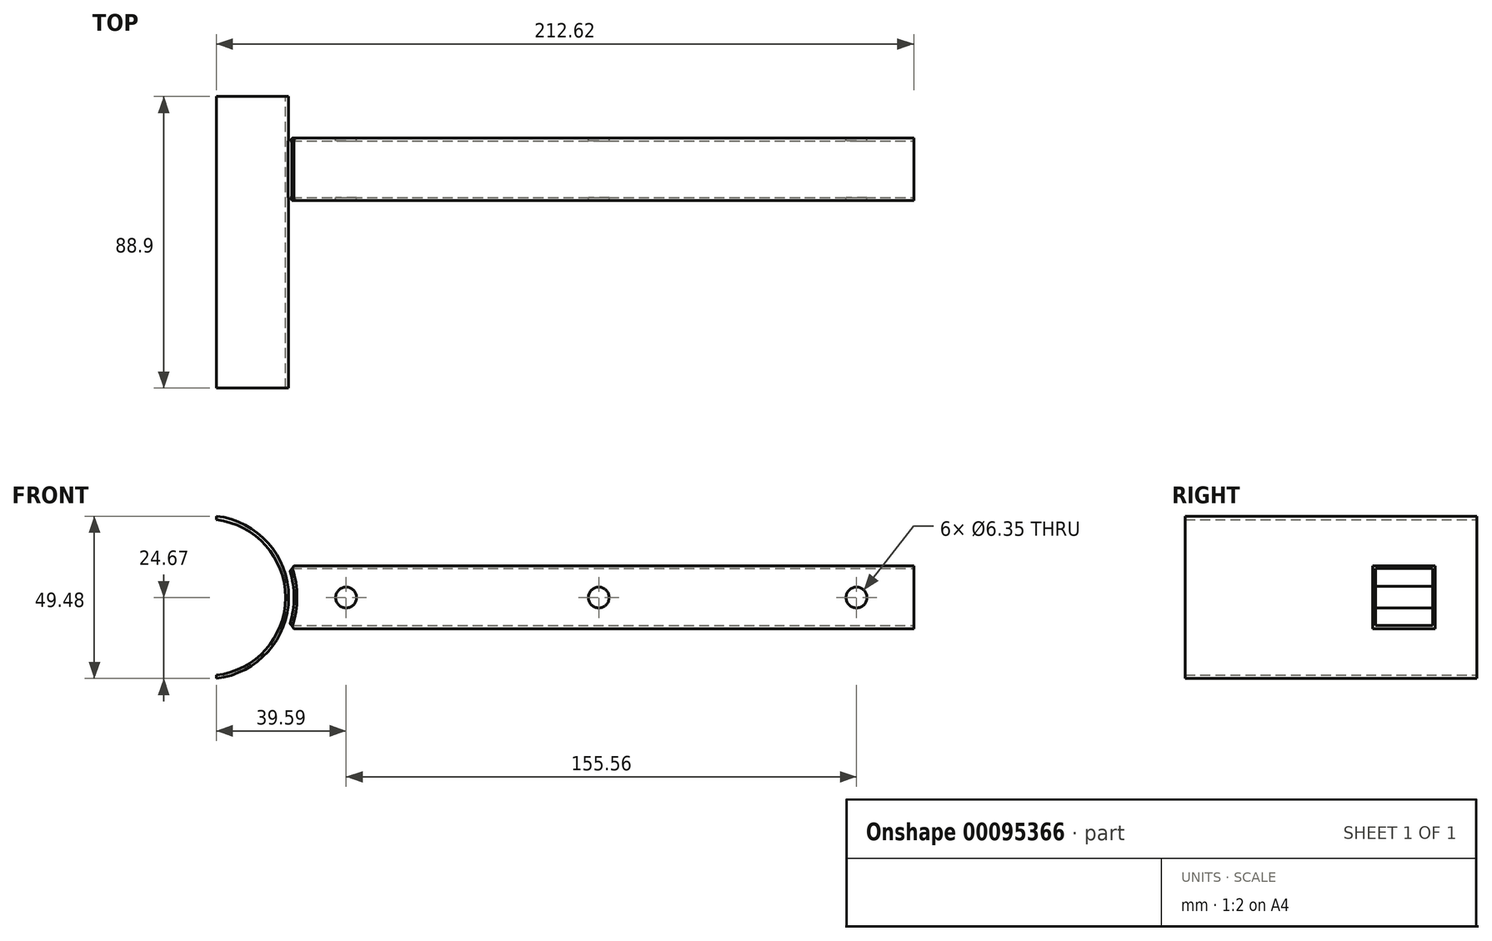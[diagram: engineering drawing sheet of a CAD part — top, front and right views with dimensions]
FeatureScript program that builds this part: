
annotation { "Feature Type Name" : "Feature", "Feature Type Description" : "" }
export const myFeature = defineFeature(function(context is Context, id is Id, definition is map)
    precondition{}
    {
        {
            var Q0;
            Q0=qCreatedBy(makeId("Front.planeOp"),FACE);
            cPlane(context, id + "F0", {"entities" : qUnion([Q0]), "cplaneType" : CPlaneType.OFFSET, "offset" : 12.7 * mm, "width" : 152.4 * mm, "height" : 152.4 * mm});
        }
        {
            var Q0;
            Q0=qCreatedBy(id+"F0.planeOp",FACE);
            var sketch = newSketch(context, id + "F1", { "sketchPlane" : qUnion([Q0])});
            skLineSegment(sketch, "E0.bottom", {"start": v(22.87, -9.48) * mm, "end": v(215.32, -9.48) * mm});
            skLineSegment(sketch, "E0.top", {"start": v(22.87, 9.62) * mm, "end": v(215.32, 9.62) * mm});
            skLineSegment(sketch, "E0.right", {"start": v(215.32, -9.48) * mm, "end": v(215.32, 9.62) * mm});
            skArc(sketch, "E1", {"start": v(22.87, -9.48) * mm, "mid": v(24.77, 0.07) * mm, "end": v(22.87, 9.62) * mm});
            skLineSegment(sketch, "E2", {"start": v(24.82, -9.48) * mm, "end": v(24.73, 9.62) * mm, "construction": true});
            skLineSegment(sketch, "E3", {"start": v(0, 0) * mm, "end": v(85.8, 0.07) * mm, "construction": true});
            skSolve(sketch);
        }
        {
            var Q0;
            Q0=makeQuery(id+"F1.imprint","IMPRINT",FACE,{"disambiguationData":[TD([[makeQuery(id+"F1.imprint","IMPRINT",EDGE,{"derivedFrom":sQuery(id+"F1.wireOp",EDGE,"E0.bottom")}),1.0]])]});
            extrude(context, id + "F2", {"entities" : qUnion([Q0]), "depth" : 19.05 * mm});
        }
        {
            var Q0;
            Q0=qCreatedBy(makeId("Front.planeOp"),FACE);
            var sketch = newSketch(context, id + "F3", { "sketchPlane" : qUnion([Q0])});
            skArc(sketch, "E4", {"start": v(2.7, -24.67) * mm, "mid": v(24.77, 0.07) * mm, "end": v(2.7, 24.81) * mm});
            skLineSegment(sketch, "E5", {"start": v(2.7, 24.81) * mm, "end": v(2.7, 24.81) * mm});
            skLineSegment(sketch, "E6", {"start": v(2.7, -24.67) * mm, "end": v(2.69, -24.62) * mm});
            skArc(sketch, "E7", {"start": v(2.7, -23.68) * mm, "mid": v(23.83, 0) * mm, "end": v(2.7, 23.68) * mm});
            skLineSegment(sketch, "E8", {"start": v(2.7, 24.81) * mm, "end": v(2.7, 23.68) * mm});
            skLineSegment(sketch, "E9", {"start": v(2.7, -24.67) * mm, "end": v(2.7, -23.68) * mm});
            skSolve(sketch);
        }
        {
            var Q0;
            Q0=makeQuery(id+"F3.imprint","IMPRINT",FACE,{"disambiguationData":[TD([[makeQuery(id+"F3.imprint","IMPRINT",EDGE,{"derivedFrom":sQuery(id+"F3.wireOp",EDGE,"E4")}),1.0]])]});
            extrude(context, id + "F4", {"entities" : qUnion([Q0]), "operationType" : NewBodyOperationType.ADD, "depth" : 88.9 * mm});
        }
        {
            var Q0;
            Q0=makeQuery(id+"F2.opExtrude","CAP_FACE",FACE,{"disambiguationData":[OSD([sQuery(id+"F1.wireOp",EDGE,"E0.bottom"),sQuery(id+"F1.wireOp",EDGE,"E0.top"),sQuery(id+"F1.wireOp",EDGE,"E0.right"),sQuery(id+"F1.wireOp",EDGE,"E1")])],"isStart":true});
            var sketch = newSketch(context, id + "F5", { "sketchPlane" : qUnion([Q0])});
            skLineSegment(sketch, "E10", {"start": v(-24.77, -9.48) * mm, "end": v(-24.77, 9.62) * mm, "construction": true});
            skSolve(sketch);
        }
        {
            var Q0;
            Q0=makeQuery(id+"F2.opExtrude","SWEPT_FACE",FACE,{"disambiguationData":[OSD([sQuery(id+"F1.wireOp",EDGE,"E0.right")])]});
            var sketch = newSketch(context, id + "F6", { "sketchPlane" : qUnion([Q0])});
            skLineSegment(sketch, "E11.bottom", {"start": v(-30.84, 8.86) * mm, "end": v(-13.54, 8.86) * mm});
            skLineSegment(sketch, "E11.top", {"start": v(-30.84, -8.54) * mm, "end": v(-13.54, -8.54) * mm});
            skLineSegment(sketch, "E11.left", {"start": v(-30.84, 8.86) * mm, "end": v(-30.84, -8.54) * mm});
            skLineSegment(sketch, "E11.right", {"start": v(-13.54, 8.86) * mm, "end": v(-13.54, -8.54) * mm});
            skSolve(sketch);
        }
        {
            var Q0;
            Q0=makeQuery(id+"F6.imprint","IMPRINT",FACE,{"disambiguationData":[TD([[makeQuery(id+"F6.imprint","IMPRINT",EDGE,{"derivedFrom":sQuery(id+"F6.wireOp",EDGE,"E11.bottom")}),-1.0]])]});
            extrude(context, id + "F7", {"entities" : qUnion([Q0]), "operationType" : NewBodyOperationType.REMOVE, "oppositeDirection" : true, "depth" : 190.77 * mm});
        }
        {
            var Q0;
            Q0=makeQuery(id+"F2.opExtrude","SWEPT_EDGE",EDGE,{"disambiguationData":[OSD([sQuery(id+"F1.wireOp",EDGE,"E0.bottom"),sQuery(id+"F1.wireOp",EDGE,"E1")])]});
            var Q1;
            Q1=makeQuery(id+"F2.opExtrude","CAP_EDGE",EDGE,{"disambiguationData":[OSD([sQuery(id+"F1.wireOp",EDGE,"E1")])],"isStart":false});
            var Q2;
            Q2=makeQuery(id+"F2.opExtrude","CAP_EDGE",EDGE,{"disambiguationData":[OSD([sQuery(id+"F1.wireOp",EDGE,"E1")])],"isStart":true});
            var Q3;
            Q3=makeQuery(id+"F2.opExtrude","SWEPT_EDGE",EDGE,{"disambiguationData":[OSD([sQuery(id+"F1.wireOp",EDGE,"E0.top"),sQuery(id+"F1.wireOp",EDGE,"E1")])]});
            chamfer(context, id + "F8", {"entities" : qUnion([Q0, Q1, Q2, Q3]), "width" : 2.54 * mm, "tangentPropagation" : true});
        }
        {
            var Q0;
            Q0=makeQuery(id+"F5.imprint","IMPRINT",FACE,{"disambiguationData":[TD([[makeQuery(id+"F5.imprint","IMPRINT",EDGE,{"derivedFrom":makeQuery(id+"F2.opExtrude","CAP_EDGE",EDGE,{"disambiguationData":[OSD([sQuery(id+"F1.wireOp",EDGE,"E0.bottom")])],"isStart":true})}),-1.0]])]});
            var sketch = newSketch(context, id + "F9", { "sketchPlane" : qUnion([Q0])});
            skCircle(sketch, "E12", {"center": v(0, 0) * mm, "radius": 244.97 * mm, "construction": true});
            skCircle(sketch, "E13", {"center": v(0, 0) * mm, "radius": 245.37 * mm});
            skLineSegment(sketch, "E14", {"start": v(-8.87, 25.42) * mm, "end": v(-86.64, -40.46) * mm});
            skLineSegment(sketch, "E15", {"start": v(-164.07, -40.4) * mm, "end": v(-86.38, 25.41) * mm});
            skLineSegment(sketch, "E16", {"start": v(-241.84, -39.05) * mm, "end": v(-165.73, 25.41) * mm});
            skPoint(sketch, "E17", {"position": v(-42.29, 0) * mm});
            skPoint(sketch, "E18", {"position": v(-119.28, 0) * mm});
            skPoint(sketch, "E19", {"position": v(-197.85, 0) * mm});
            skSolve(sketch);
        }
        {
            var Q0;
            Q0=sQuery(id+"F9.wireOp",VERTEX,"E17");
            var Q1;
            Q1=sQuery(id+"F9.wireOp",VERTEX,"E18");
            var Q2;
            Q2=sQuery(id+"F9.wireOp",VERTEX,"E19");
            var Q3;
            Q3=makeQuery(id+"F2.opExtrude","SWEPT_BODY",BODY,{"disambiguationData":[OSD([sQuery(id+"F1.wireOp",EDGE,"E0.bottom"),sQuery(id+"F1.wireOp",EDGE,"E0.top"),sQuery(id+"F1.wireOp",EDGE,"E0.right"),sQuery(id+"F1.wireOp",EDGE,"E1")])]});
            hole(context, id + "F10", {"style" : HoleStyle.SIMPLE, "endStyle" : HoleEndStyle.THROUGH, "holeDiameter" : 6.35 * mm, "locations" : qUnion([Q0, Q1, Q2]), "scope" : qUnion([Q3]), "isTappedThrough" : true});
        }
    });
